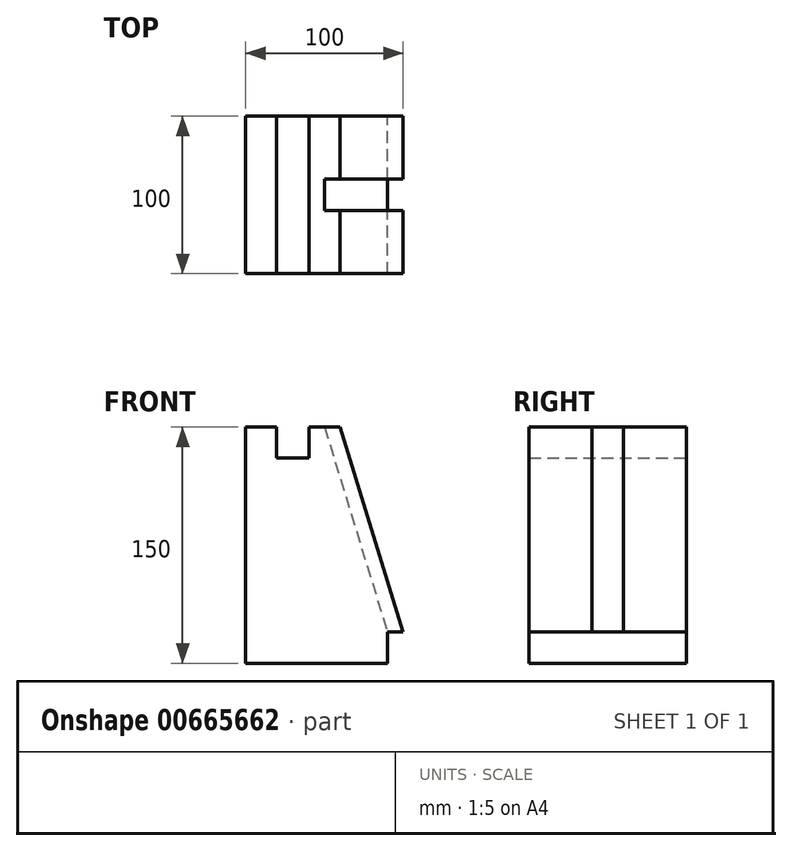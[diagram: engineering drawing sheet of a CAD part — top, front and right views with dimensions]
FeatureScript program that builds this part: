
annotation { "Feature Type Name" : "Feature", "Feature Type Description" : "" }
export const myFeature = defineFeature(function(context is Context, id is Id, definition is map)
    precondition{}
    {
        {
            var Q0;
            Q0=qCreatedBy(makeId("Front.planeOp"),FACE);
            var sketch = newSketch(context, id + "F0", { "sketchPlane" : qUnion([Q0])});
            skLineSegment(sketch, "E0", {"start": v(0, 0) * mm, "end": v(0, 150) * mm});
            skLineSegment(sketch, "E1", {"start": v(0, 150) * mm, "end": v(60, 150) * mm});
            skLineSegment(sketch, "E2", {"start": v(0, 0) * mm, "end": v(100, 0) * mm});
            skLineSegment(sketch, "E3", {"start": v(100, 0) * mm, "end": v(100, 20) * mm});
            skLineSegment(sketch, "E4", {"start": v(100, 20) * mm, "end": v(60, 150) * mm});
            skLineSegment(sketch, "E5", {"start": v(0, 150) * mm, "end": v(19.66, 150) * mm});
            skLineSegment(sketch, "E6", {"start": v(19.66, 150) * mm, "end": v(19.66, 130.43) * mm});
            skLineSegment(sketch, "E7", {"start": v(19.66, 130.43) * mm, "end": v(40.1, 130.43) * mm});
            skLineSegment(sketch, "E8", {"start": v(40.1, 150) * mm, "end": v(40.1, 130.43) * mm});
            skSolve(sketch);
        }
        {
            var Q0;
            Q0=makeQuery(id+"F0.imprint","IMPRINT",FACE,{"disambiguationData":[TD([[makeQuery(id+"F0.imprint","IMPRINT",EDGE,{"derivedFrom":sQuery(id+"F0.wireOp",EDGE,"E0")}),-1.0]])]});
            extrude(context, id + "F1", {"entities" : qUnion([Q0]), "depth" : 100 * mm, "offsetDistance" : 25 * mm});
        }
        {
            var Q0;
            Q0=makeQuery(id+"F1.opExtrude","SWEPT_FACE",FACE,{"disambiguationData":[OSD([sQuery(id+"F0.wireOp",EDGE,"E4")])]});
            var sketch = newSketch(context, id + "F2", { "sketchPlane" : qUnion([Q0])});
            skLineSegment(sketch, "E9", {"start": v(-100, 125.72) * mm, "end": v(-60, 125.72) * mm});
            skLineSegment(sketch, "E10", {"start": v(-60, 125.72) * mm, "end": v(-40, 125.72) * mm});
            skLineSegment(sketch, "E11", {"start": v(-40, 125.72) * mm, "end": v(0, 125.72) * mm});
            skLineSegment(sketch, "E12", {"start": v(-60, 125.72) * mm, "end": v(-60, -30.49) * mm});
            skLineSegment(sketch, "E13", {"start": v(-40, 125.72) * mm, "end": v(-40, -30.07) * mm});
            skSolve(sketch);
        }
        {
            var Q0;
            Q0=makeQuery(id+"F1.opExtrude","SWEPT_FACE",FACE,{"disambiguationData":[OSD([sQuery(id+"F0.wireOp",EDGE,"E3")])]});
            var Q1;
            {var subQ0=sQuery(id+"F2.wireOp",EDGE,"E10");Q1=makeQuery(id+"F2.imprint","IMPRINT",FACE,{"disambiguationData":[TD([[makeQuery(id+"F2.imprint","IMPRINT",EDGE,{"derivedFrom":subQ0}),-1.0]])]});}
            extrude(context, id + "F3", {"entities" : qUnion([Q0, Q1]), "operationType" : NewBodyOperationType.REMOVE, "oppositeDirection" : true, "depth" : 10 * mm, "offsetDistance" : 25 * mm});
        }
    });
